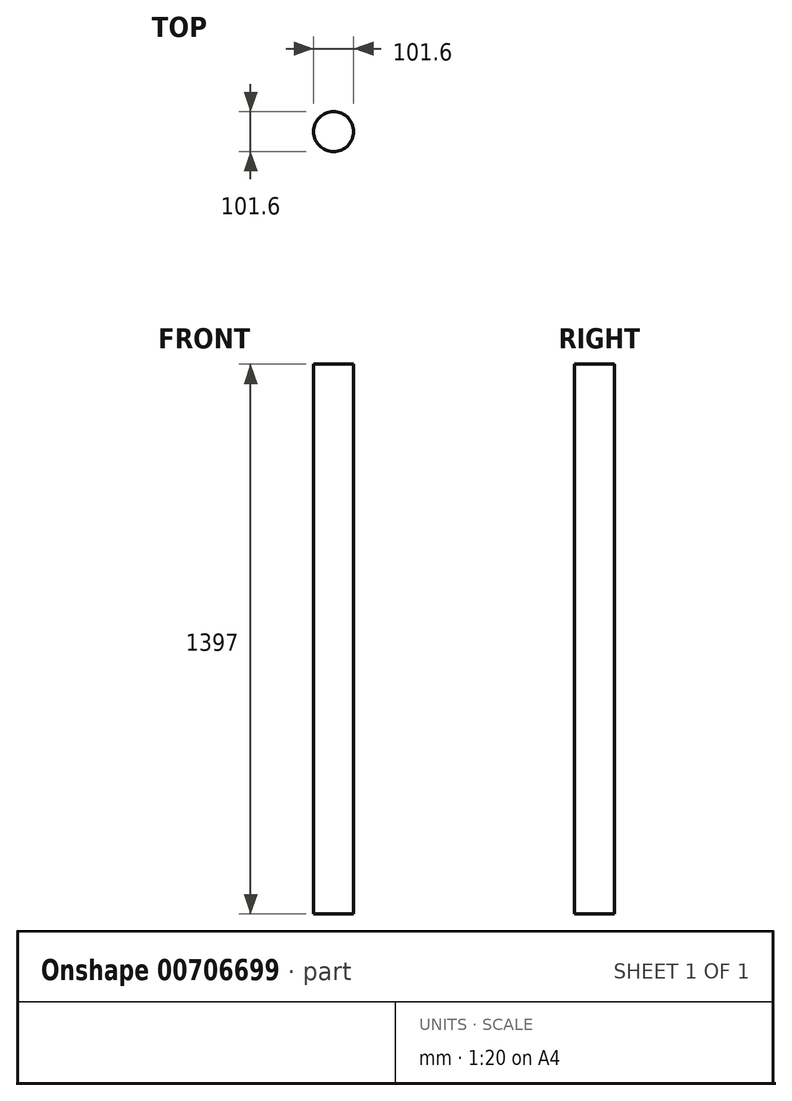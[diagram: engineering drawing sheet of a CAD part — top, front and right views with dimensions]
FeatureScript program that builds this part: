
annotation { "Feature Type Name" : "Feature", "Feature Type Description" : "" }
export const myFeature = defineFeature(function(context is Context, id is Id, definition is map)
    precondition{}
    {
        {
            var Q0;
            Q0=qCreatedBy(makeId("Top.planeOp"),FACE);
            var sketch = newSketch(context, id + "F0", { "sketchPlane" : qUnion([Q0])});
            skCircle(sketch, "E0", {"center": v(0, 0) * mm, "radius": 50.8 * mm});
            skSolve(sketch);
        }
        {
            var Q0;
            Q0=makeQuery(id+"F0.imprint","IMPRINT",FACE,{"disambiguationData":[TD([[makeQuery(id+"F0.imprint","IMPRINT",EDGE,{"derivedFrom":sQuery(id+"F0.wireOp",EDGE,"E0")}),1.0]])]});
            extrude(context, id + "F1", {"entities" : qUnion([Q0]), "depth" : 1397 * mm, "offsetDistance" : 25.4 * mm});
        }
        {
            var Q0;
            Q0=makeQuery(id+"F1.opExtrude","CAP_FACE",FACE,{"disambiguationData":[OSD([sQuery(id+"F0.wireOp",EDGE,"E0")])],"isStart":true});
            var sketch = newSketch(context, id + "F2", { "sketchPlane" : qUnion([Q0])});
            skLineSegment(sketch, "E1.bottom", {"start": v(0.01, 50.8) * mm, "end": v(-0.01, 50.8) * mm});
            skLineSegment(sketch, "E1.top", {"start": v(0.01, -50.8) * mm, "end": v(-0.01, -50.8) * mm});
            skLineSegment(sketch, "E1.left", {"start": v(0.01, 50.8) * mm, "end": v(0.01, -50.8) * mm});
            skLineSegment(sketch, "E1.right", {"start": v(-0.01, 50.8) * mm, "end": v(-0.01, -50.8) * mm});
            skPoint(sketch, "E1.middle", {"position": v(0, 0) * mm});
            skSolve(sketch);
        }
    });
